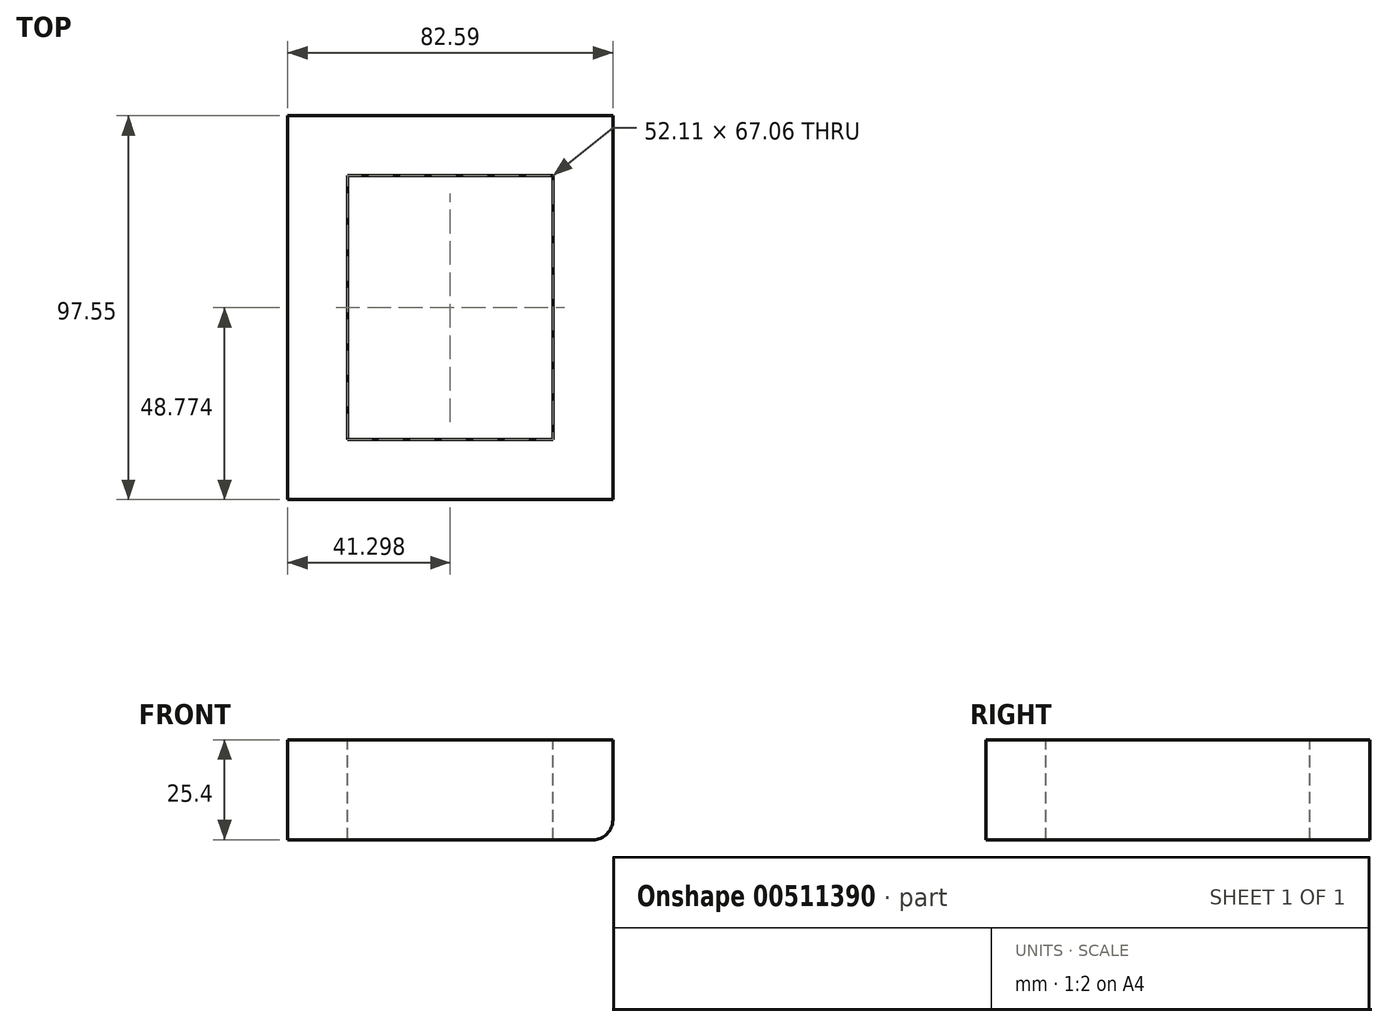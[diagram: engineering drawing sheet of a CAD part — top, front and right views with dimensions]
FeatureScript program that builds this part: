
annotation { "Feature Type Name" : "Feature", "Feature Type Description" : "" }
export const myFeature = defineFeature(function(context is Context, id is Id, definition is map)
    precondition{}
    {
        {
            var Q0;
            Q0=qCreatedBy(makeId("Top.planeOp"),FACE);
            var sketch = newSketch(context, id + "F0", { "sketchPlane" : qUnion([Q0])});
            skLineSegment(sketch, "E0.bottom", {"start": v(-52.64, -43.99) * mm, "end": v(29.95, -43.99) * mm});
            skLineSegment(sketch, "E0.top", {"start": v(-52.64, 53.56) * mm, "end": v(29.95, 53.56) * mm});
            skLineSegment(sketch, "E0.left", {"start": v(-52.64, -43.99) * mm, "end": v(-52.64, 53.56) * mm});
            skLineSegment(sketch, "E0.right", {"start": v(29.95, -43.99) * mm, "end": v(29.95, 53.56) * mm});
            skSolve(sketch);
        }
        {
            var Q0;
            Q0 = qSketchRegion(id + "F0", true);
            extrude(context, id + "F1", {"entities" : qUnion([Q0]), "depth" : 25.4 * mm});
        }
        {
            var Q0;
            Q0=makeQuery(id+"F1.opExtrude","CAP_FACE",FACE,{"disambiguationData":[OSD([sQuery(id+"F0.wireOp",EDGE,"E0.bottom"),sQuery(id+"F0.wireOp",EDGE,"E0.top"),sQuery(id+"F0.wireOp",EDGE,"E0.left"),sQuery(id+"F0.wireOp",EDGE,"E0.right")])],"isStart":false});
            var sketch = newSketch(context, id + "F2", { "sketchPlane" : qUnion([Q0])});
            skLineSegment(sketch, "E1.bottom", {"start": v(14.71, 38.32) * mm, "end": v(-37.4, 38.32) * mm});
            skLineSegment(sketch, "E1.top", {"start": v(14.71, -28.75) * mm, "end": v(-37.4, -28.75) * mm});
            skLineSegment(sketch, "E1.left", {"start": v(14.71, 38.32) * mm, "end": v(14.71, -28.75) * mm});
            skLineSegment(sketch, "E1.right", {"start": v(-37.4, 38.32) * mm, "end": v(-37.4, -28.75) * mm});
            skSolve(sketch);
        }
        {
            var Q0;
            Q0 = qSketchRegion(id + "F2", true);
            extrude(context, id + "F3", {"entities" : qUnion([Q0]), "operationType" : NewBodyOperationType.REMOVE, "oppositeDirection" : true, "depth" : 25.4 * mm});
        }
        {
            var Q0;
            Q0=makeQuery(id+"F1.opExtrude","CAP_EDGE",EDGE,{"disambiguationData":[OSD([sQuery(id+"F0.wireOp",EDGE,"E0.right")])],"isStart":true});
            fillet(context, id + "F4", {"entities" : qUnion([Q0]), "radius" : 5.08 * mm, "tangentPropagation" : true, "allowEdgeOverflow" : false});
        }
    });
